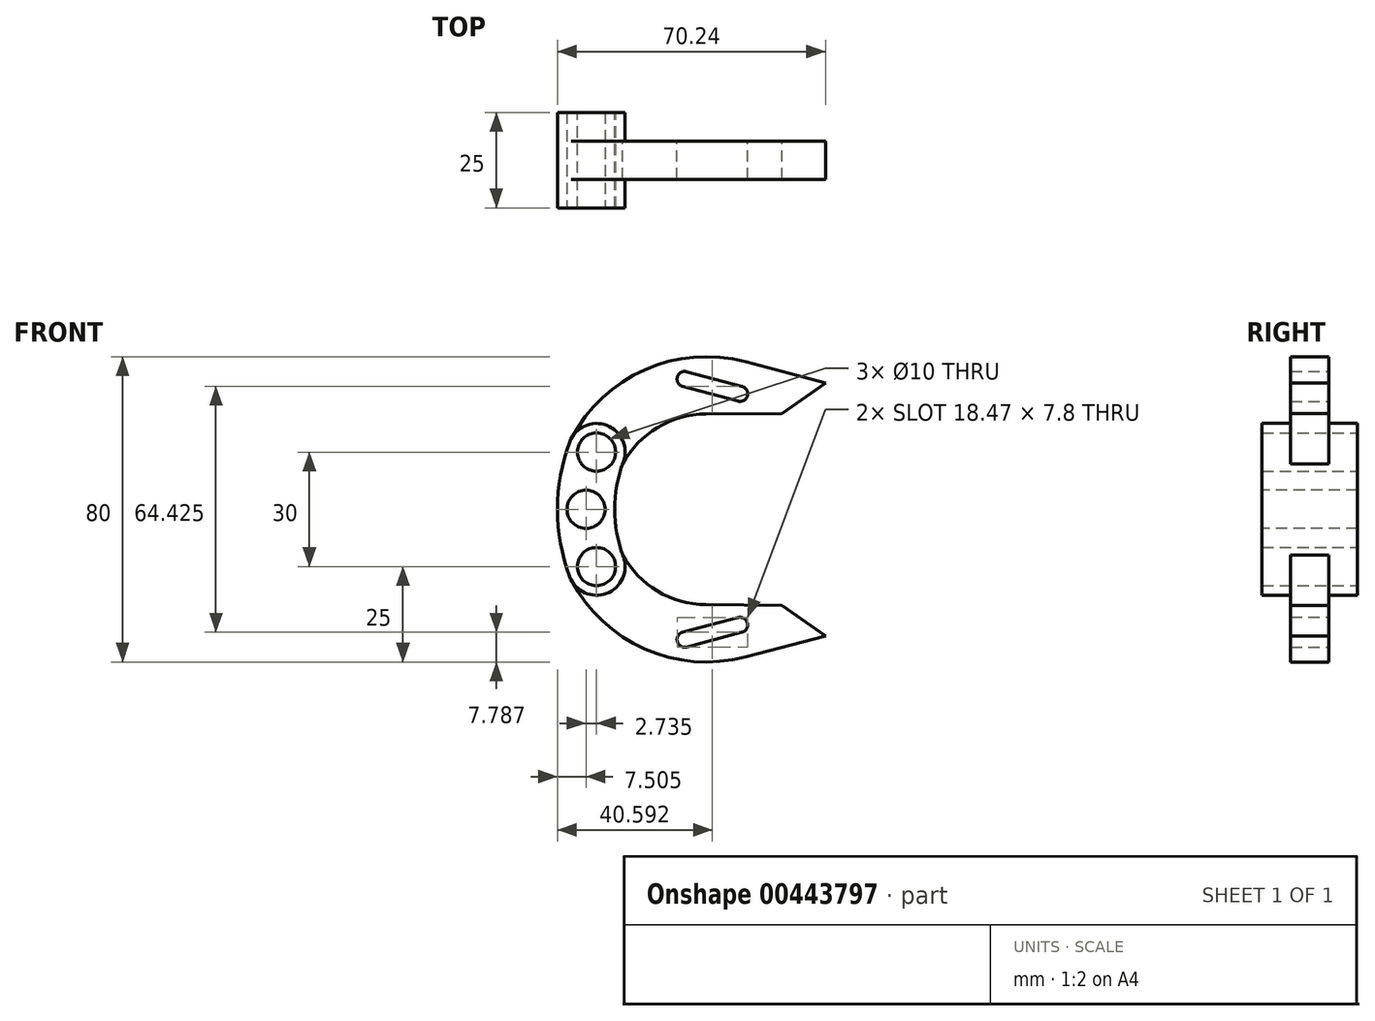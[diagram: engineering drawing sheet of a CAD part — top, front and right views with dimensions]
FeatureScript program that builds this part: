
annotation { "Feature Type Name" : "Feature", "Feature Type Description" : "" }
export const myFeature = defineFeature(function(context is Context, id is Id, definition is map)
    precondition{}
    {
        {
            var Q0;
            Q0=qCreatedBy(makeId("Front.planeOp"),FACE);
            var sketch = newSketch(context, id + "F0", { "sketchPlane" : qUnion([Q0])});
            skLineSegment(sketch, "E0", {"start": v(0, 0) * mm, "end": v(0, 15) * mm});
            skLineSegment(sketch, "E1", {"start": v(0, 15) * mm, "end": v(0, -15) * mm, "construction": true});
            skLineSegment(sketch, "E2", {"start": v(0, 0) * mm, "end": v(80, 0) * mm, "construction": true});
            skCircle(sketch, "E3", {"center": v(0, 15) * mm, "radius": 5 * mm});
            skCircle(sketch, "E4", {"center": v(0, -15) * mm, "radius": 5 * mm});
            skArc(sketch, "E5.0", {"start": v(7.02, 12.35) * mm, "mid": v(2.65, 22.02) * mm, "end": v(-7.02, 17.65) * mm});
            skArc(sketch, "E6.0", {"start": v(-7.02, -17.65) * mm, "mid": v(2.65, -22.02) * mm, "end": v(7.02, -12.35) * mm});
            skArc(sketch, "E7", {"start": v(-7.02, 17.65) * mm, "mid": v(-10.24, 0) * mm, "end": v(-7.02, -17.65) * mm});
            skArc(sketch, "E8", {"start": v(7.02, 12.35) * mm, "mid": v(4.76, 0) * mm, "end": v(7.02, -12.35) * mm});
            skSolve(sketch);
        }
        {
            var Q0;
            Q0=qCreatedBy(makeId("Front.planeOp"),FACE);
            var sketch = newSketch(context, id + "F1", { "sketchPlane" : qUnion([Q0])});
            skCircle(sketch, "E9.0", {"center": v(0, 15) * mm, "radius": 5 * mm});
            skCircle(sketch, "E10", {"center": v(0, 15) * mm, "radius": 7.5 * mm});
            skArc(sketch, "E11", {"start": v(39.05, 38.67) * mm, "mid": v(12.65, 36.58) * mm, "end": v(-6.65, 18.46) * mm});
            skArc(sketch, "E12", {"start": v(28.66, 25) * mm, "mid": v(15.79, 21.33) * mm, "end": v(6.65, 11.54) * mm});
            skLineSegment(sketch, "E13", {"start": v(28.66, 25) * mm, "end": v(48.66, 25.14) * mm});
            skLineSegment(sketch, "E14", {"start": v(39.05, 38.67) * mm, "end": v(60, 33.14) * mm});
            skLineSegment(sketch, "E15", {"start": v(60, 33.14) * mm, "end": v(48.66, 25.14) * mm});
            skLineSegment(sketch, "E16", {"start": v(39.05, 38.67) * mm, "end": v(37.6, 30.3) * mm, "construction": true});
            skLineSegment(sketch, "E17", {"start": v(37.6, 30.3) * mm, "end": v(23.1, 34.13) * mm, "construction": true});
            skArc(sketch, "E18", {"start": v(23.61, 36.06) * mm, "mid": v(21.17, 34.64) * mm, "end": v(22.59, 32.2) * mm});
            skArc(sketch, "E19", {"start": v(37.1, 28.36) * mm, "mid": v(39.56, 29.87) * mm, "end": v(37.94, 32.27) * mm});
            skLineSegment(sketch, "E20", {"start": v(23.61, 36.06) * mm, "end": v(38.11, 32.23) * mm});
            skLineSegment(sketch, "E21", {"start": v(22.59, 32.2) * mm, "end": v(37.1, 28.36) * mm});
            skLineSegment(sketch, "E22.MirrorCS", {"start": v(39.05, -38.67) * mm, "end": v(60, -33.14) * mm});
            skCircle(sketch, "E23.MirrorC", {"center": v(0, -15) * mm, "radius": 7.5 * mm});
            skLineSegment(sketch, "E24.MirrorCS", {"start": v(39.05, -38.67) * mm, "end": v(37.6, -30.3) * mm, "construction": true});
            skLineSegment(sketch, "E25.MirrorCS", {"start": v(37.6, -30.3) * mm, "end": v(23.1, -34.13) * mm, "construction": true});
            skLineSegment(sketch, "E26.MirrorCS", {"start": v(22.59, -32.2) * mm, "end": v(37.1, -28.36) * mm});
            skArc(sketch, "E27.MirrorCS", {"start": v(23.61, -36.06) * mm, "mid": v(21.17, -34.64) * mm, "end": v(22.59, -32.2) * mm});
            skLineSegment(sketch, "E28.MirrorCS", {"start": v(23.61, -36.06) * mm, "end": v(38.11, -32.23) * mm});
            skLineSegment(sketch, "E29.MirrorCS", {"start": v(60, -33.14) * mm, "end": v(48.66, -25.14) * mm});
            skArc(sketch, "E30.MirrorCS", {"start": v(39.05, -38.67) * mm, "mid": v(12.65, -36.58) * mm, "end": v(-6.65, -18.46) * mm});
            skLineSegment(sketch, "E31.MirrorCS", {"start": v(28.66, -25) * mm, "end": v(48.66, -25.14) * mm});
            skArc(sketch, "E32.MirrorCS", {"start": v(28.66, -25) * mm, "mid": v(15.79, -21.33) * mm, "end": v(6.65, -11.54) * mm});
            skCircle(sketch, "E33.MirrorC", {"center": v(0, -15) * mm, "radius": 5 * mm});
            skArc(sketch, "E34.MirrorCS", {"start": v(37.1, -28.36) * mm, "mid": v(39.56, -29.87) * mm, "end": v(37.94, -32.27) * mm});
            skSolve(sketch);
        }
        {
            var Q0;
            Q0 = qSketchRegion(id + "F0", true);
            extrude(context, id + "F2", {"entities" : qUnion([Q0]), "endBound" : BoundingType.SYMMETRIC, "depth" : 25 * mm});
        }
        {
            var Q0;
            Q0 = qSketchRegion(id + "F1", true);
            extrude(context, id + "F3", {"entities" : qUnion([Q0]), "operationType" : NewBodyOperationType.ADD, "endBound" : BoundingType.SYMMETRIC, "depth" : 10 * mm});
        }
        {
            var Q0;
            Q0=makeQuery(id+"F2.opExtrude","CAP_FACE",FACE,{"disambiguationData":[OSD([sQuery(id+"F0.wireOp",EDGE,"E3"),sQuery(id+"F0.wireOp",EDGE,"E4"),sQuery(id+"F0.wireOp",EDGE,"E5.0"),sQuery(id+"F0.wireOp",EDGE,"E6.0"),sQuery(id+"F0.wireOp",EDGE,"E7"),sQuery(id+"F0.wireOp",EDGE,"E8")])],"isStart":false});
            var sketch = newSketch(context, id + "F4", { "sketchPlane" : qUnion([Q0])});
            skArc(sketch, "E35", {"start": v(0, 15) * mm, "mid": v(-2.74, 0) * mm, "end": v(0, -15) * mm, "construction": true});
            skCircle(sketch, "E36", {"center": v(-2.74, 0) * mm, "radius": 5 * mm});
            skSolve(sketch);
        }
        {
            var Q0;
            Q0 = qSketchRegion(id + "F4", true);
            extrude(context, id + "F5", {"entities" : qUnion([Q0]), "operationType" : NewBodyOperationType.REMOVE, "endBound" : BoundingType.THROUGH_ALL, "oppositeDirection" : true, "depth" : 25 * mm});
        }
    });
